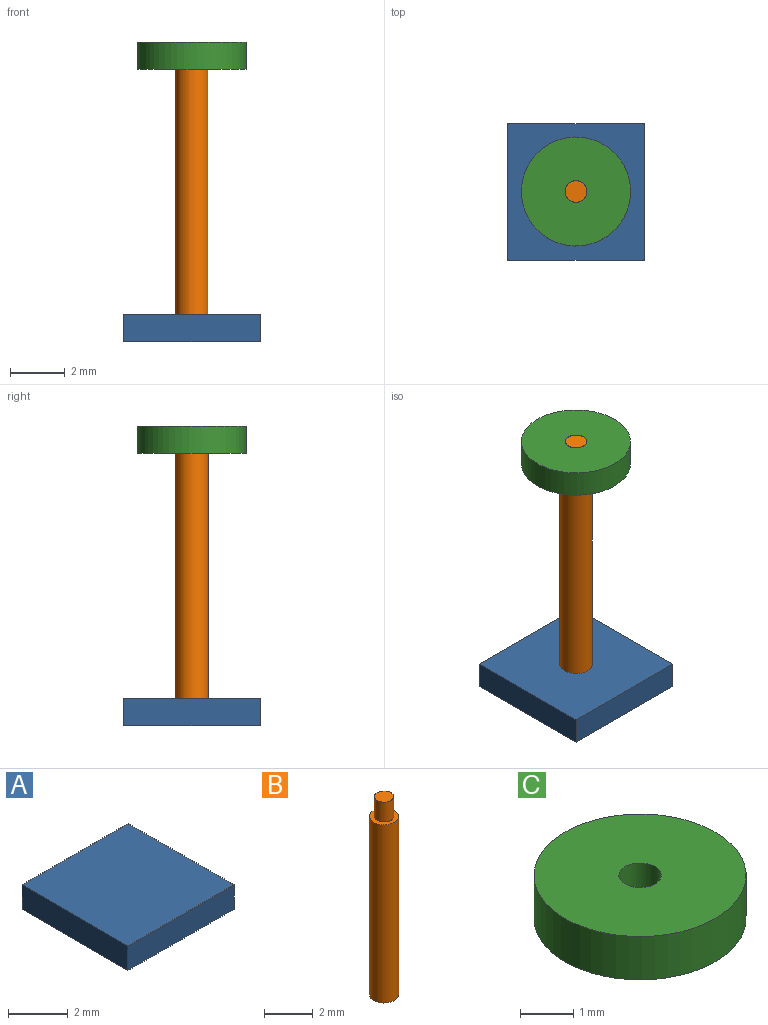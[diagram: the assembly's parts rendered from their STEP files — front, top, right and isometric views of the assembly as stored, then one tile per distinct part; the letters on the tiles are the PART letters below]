
ASSEMBLY  parts=3 mates=2
PART A: 6 faces, bbox 5x5x1 mm
  f0: plane 5x1mm, normal (-1,0,0), area 5mm2, adj f1,f3,f4,f5
  f1: plane 5x1mm, normal (0,-1,0), area 5mm2, adj f0,f2,f4,f5
  f2: plane 5x1mm, normal (1,0,0), area 5mm2, adj f1,f3,f4,f5
  f3: plane 5x1mm, normal (0,1,0), area 5mm2, adj f0,f2,f4,f5
  f4: plane 5x5mm, normal (0,0,1), area 25mm2, adj f0,f1,f2,f3
  f5: plane 5x5mm, normal (0,0,-1), area 25mm2, adj f0,f1,f2,f3
PART B: 5 faces, bbox 1.2x1.2x10 mm
  f0: plane 1.2x1.2mm, normal (0,0,-1), area 1.1mm2, adj f1
  f1: cylinder r=0.6mm len=9mm, axis (0,0,-1), area 33.9mm2, adj f0,f2
  f2: plane 1.2x1.2mm, normal (0,0,1), area 0.6mm2, adj f1,f3
  f3: cylinder r=0.4mm len=1mm, axis (0,0,-1), area 2.5mm2, adj f2,f4
  f4: plane 0.8x0.8mm, normal (0,0,1), area 0.5mm2, adj f3
PART C: 4 faces, bbox 4x4x1 mm
  f0: cylinder r=0.4mm len=1mm, axis (0,0,-1), area 2.5mm2, adj f2,f3
  f1: cylinder r=2mm len=4mm, axis (0,0,-1), area 12.6mm2, adj f2,f3
  f2: plane 4x4mm, normal (0,0,1), area 12.1mm2, adj f0,f1
  f3: plane 4x4mm, normal (0,0,-1), area 12.1mm2, adj f0,f1
PLACE A t=(0.2,2.94,-5.52)mm
PLACE B t=(2.7,5.44,-4.52)mm
PLACE C t=(2.7,5.44,4.48)mm
MATE revolute B.f1 <-> C.f1  axis (0,0,1) through (2.7,5.44,5.48)mm
MATE fastened B.f1 <-> A.f4  axis (0,0,-1) through (2.7,5.44,-4.52)mm
